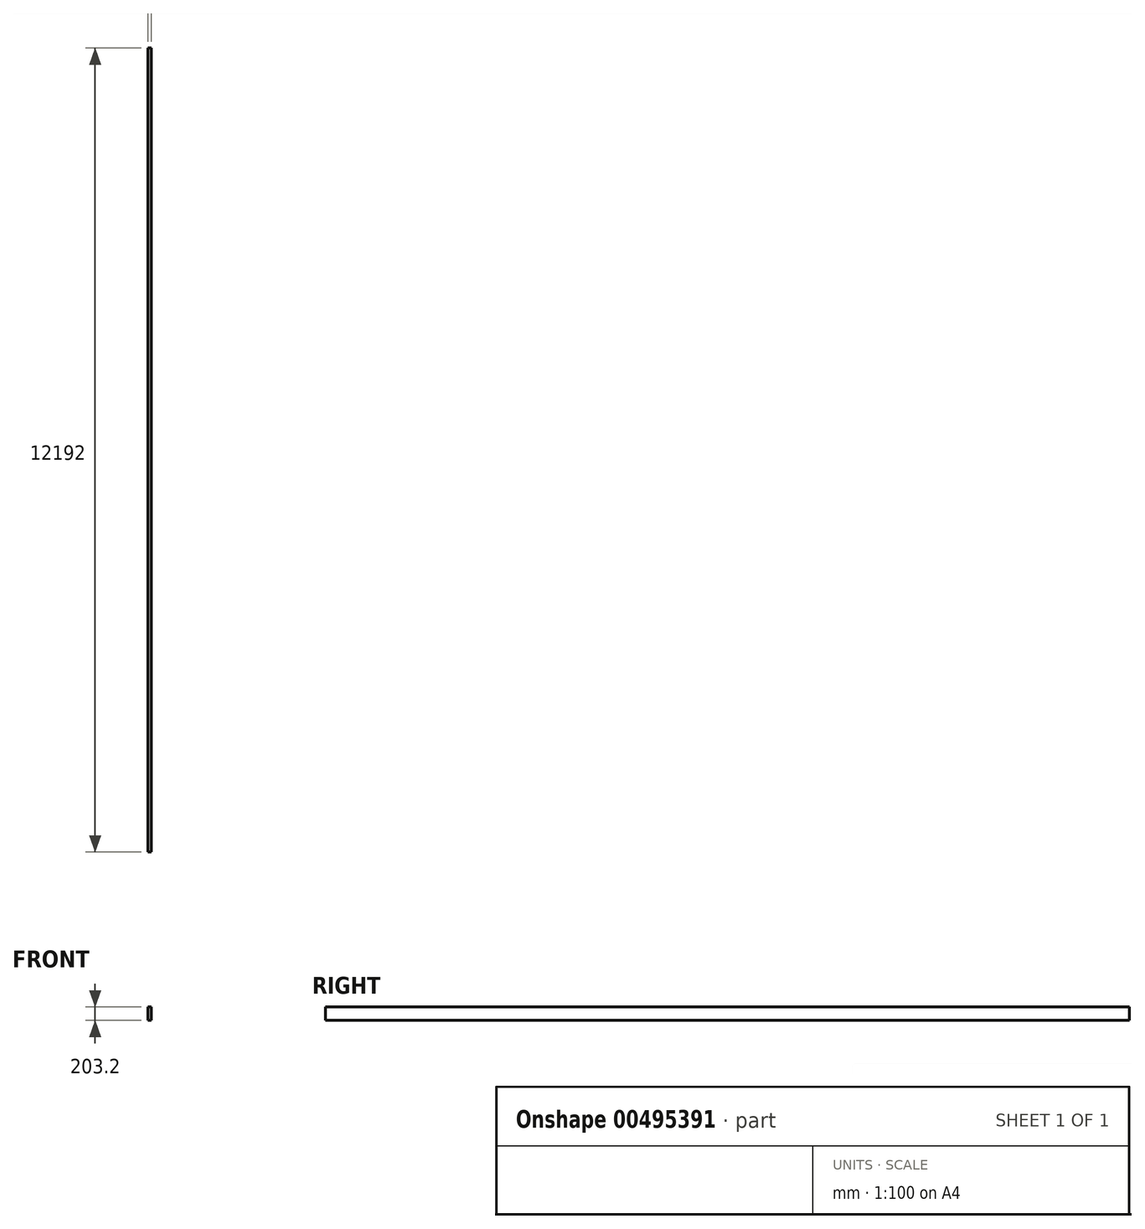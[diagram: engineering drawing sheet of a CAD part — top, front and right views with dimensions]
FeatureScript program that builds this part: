
annotation { "Feature Type Name" : "Feature", "Feature Type Description" : "" }
export const myFeature = defineFeature(function(context is Context, id is Id, definition is map)
    precondition{}
    {
        {
            var Q0;
            Q0=qCreatedBy(makeId("Front.planeOp"),FACE);
            var sketch = newSketch(context, id + "F0", { "sketchPlane" : qUnion([Q0])});
            skLineSegment(sketch, "E0.bottom", {"start": v(0, 0) * mm, "end": v(50.8, 0) * mm});
            skLineSegment(sketch, "E0.top", {"start": v(0, 203.2) * mm, "end": v(50.8, 203.2) * mm});
            skLineSegment(sketch, "E0.left", {"start": v(0, 0) * mm, "end": v(0, 203.2) * mm});
            skLineSegment(sketch, "E0.right", {"start": v(50.8, 0) * mm, "end": v(50.8, 203.2) * mm});
            skSolve(sketch);
        }
        {
            var Q0;
            Q0 = qSketchRegion(id + "F0", true);
            extrude(context, id + "F1", {"entities" : qUnion([Q0]), "depth" : 12192 * mm, "offsetDistance" : 25.4 * mm});
        }
    });
